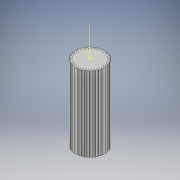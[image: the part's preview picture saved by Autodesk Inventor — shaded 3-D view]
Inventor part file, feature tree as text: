
AUTODESK INVENTOR PART (.ipt)
format: ipt  version: 2019.3 (Build 233278000, 278)  size: 697,344 bytes
history: native  units: mm
features: other x2, extrude x1
ambient origin geometry x8: Origin, YZ Plane, XZ Plane, XY Plane, X Axis, Y Axis, Z Axis, Center Point
bodies: Body1 (feature_tree)
feature tree (3):
  extrude  "Extrusion2"  Depth=5.047545mm
  other  "Work Axis1"
  other  "Work Point1"
